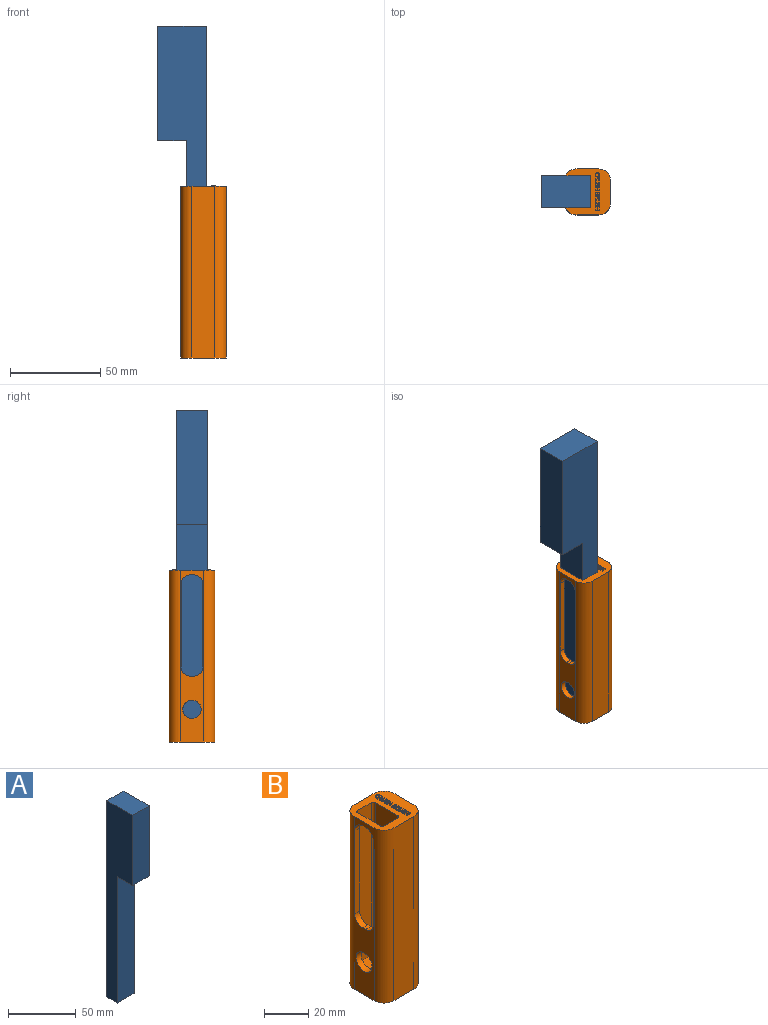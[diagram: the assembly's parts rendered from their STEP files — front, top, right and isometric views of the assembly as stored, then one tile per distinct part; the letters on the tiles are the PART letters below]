
ASSEMBLY  parts=2 mates=1
PART A: 8 faces, bbox 17.5x27x177.8 mm
  f0: plane 114.3x17.46mm, normal (0,-1,0), area 1996mm2, adj f1,f3,f5,f6
  f1: plane 177.8x26.99mm, normal (1,0,0), area 2983.9mm2, adj f0,f2,f4,f5,f6,f7
  f2: plane 177.8x17.46mm, normal (0,1,0), area 3104.8mm2, adj f1,f3,f4,f5
  f3: plane 177.8x26.99mm, normal (-1,0,0), area 2983.9mm2, adj f0,f2,f4,f5,f6,f7
  f4: plane 26.99x17.46mm, normal (0,0,1), area 471.3mm2, adj f1,f2,f3,f7
  f5: plane 17.46x11.11mm, normal (0,0,-1), area 194.1mm2, adj f0,f1,f2,f3
  f6: plane 17.46x15.88mm, normal (0,0,-1), area 277.2mm2, adj f0,f1,f3,f7
  f7: plane 63.5x17.46mm, normal (0,-1,0), area 1108.9mm2, adj f1,f3,f4,f6
PART B: 235 faces, bbox 25.4x25.4x95.8 mm
  f0: plane 95.25x12.7mm, normal (0,1,0), area 1137.1mm2, adj f1,f7,f33,f34,f228,f229,f230,f231
  f1: plane 25.4x25.4mm, normal (0,0,1), area 406.4mm2, adj f0,f3,f4,f5,f6,f8,f9,f10
  f2: cylinder r=1.91mm len=4.75mm, axis (1,0,0), area 56.9mm2, adj f6,f16
  f3: plane 95.25x12.7mm, normal (-1,0,0), area 479.9mm2, adj f1,f7,f12,f13,f14,f15,f27,f28
  f4: plane 84.14x14.48mm, normal (1,0,0), area 488.3mm2, adj f1,f11,f12,f13,f14,f15,f24,f25
  f5: plane 95.25x12.7mm, normal (0,-1,0), area 1209.7mm2, adj f1,f7,f31,f32
  f6: plane 95.25x12.7mm, normal (1,0,0), area 1198.3mm2, adj f1,f2,f7,f32,f33
  f7: plane 25.4x25.4mm, normal (0,0,-1), area 573.6mm2, adj f0,f3,f5,f6,f31,f32,f33,f34
  f8: plane 84.14x14.48mm, normal (-1,0,0), area 1157.3mm2, adj f1,f11,f17,f18,f19,f20,f21,f22
  f9: plane 84.14x8.59mm, normal (0,-1,0), area 722.3mm2, adj f1,f11,f23,f24
  f10: plane 84.14x8.59mm, normal (0,1,0), area 722.3mm2, adj f1,f11,f25,f26
  f11: plane 17.02x11.13mm, normal (0,0,1), area 187.9mm2, adj f4,f8,f9,f10,f23,f24,f25,f26
  f12: plane 3.18x1.78mm, normal (0,0,1), area 5.6mm2, adj f3,f4,f27,f28
  f13: plane 46.04x3.18mm, normal (0,-1,0), area 146.2mm2, adj f3,f4,f27,f29
  f14: plane 46.04x3.18mm, normal (0,1,0), area 146.2mm2, adj f3,f4,f28,f30
  f15: plane 3.18x1.78mm, normal (0,0,-1), area 5.6mm2, adj f3,f4,f29,f30
  f16: plane 9.68x8.38mm, normal (-1,0,0), area 49.4mm2, adj f2,f17,f18,f19,f20,f21,f22
  f17: plane 6.35x4.84mm, normal (0,1,0), area 30.7mm2, adj f8,f16,f18,f22
  f18: plane 6.35x4.19mm, normal (0,0.5,-0.87), area 30.7mm2, adj f8,f16,f17,f19
  f19: plane 6.35x4.19mm, normal (0,-0.5,-0.87), area 30.7mm2, adj f8,f16,f18,f20
  f20: plane 6.35x4.84mm, normal (0,-1,0), area 30.7mm2, adj f8,f16,f19,f21
  f21: plane 6.35x4.19mm, normal (0,-0.5,0.87), area 30.7mm2, adj f8,f16,f20,f22
  f22: plane 6.35x4.19mm, normal (0,0.5,0.87), area 30.7mm2, adj f8,f16,f17,f21
  f23: cylinder r=1.27mm len=84.14mm, axis (0,0,-1), area 167.8mm2, adj f1,f8,f9,f11
  f24: cylinder r=1.27mm len=84.14mm, axis (0,0,1), area 167.8mm2, adj f1,f4,f9,f11
  f25: cylinder r=1.27mm len=84.14mm, axis (0,0,-1), area 167.8mm2, adj f1,f4,f10,f11
  f26: cylinder r=1.27mm len=84.14mm, axis (0,0,1), area 167.8mm2, adj f1,f8,f10,f11
  f27: cylinder r=5.08mm len=5.08mm, axis (1,0,0), area 25.3mm2, adj f3,f4,f12,f13
  f28: cylinder r=5.08mm len=5.08mm, axis (-1,0,0), area 25.3mm2, adj f3,f4,f12,f14
  f29: cylinder r=5.08mm len=5.08mm, axis (-1,0,0), area 25.3mm2, adj f3,f4,f13,f15
  f30: cylinder r=5.08mm len=5.08mm, axis (1,0,0), area 25.3mm2, adj f3,f4,f14,f15
  f31: cylinder r=6.35mm len=95.25mm, axis (0,0,1), area 950.1mm2, adj f1,f3,f5,f7
  f32: cylinder r=6.35mm len=95.25mm, axis (0,0,-1), area 950.1mm2, adj f1,f5,f6,f7
  f33: cylinder r=6.35mm len=95.25mm, axis (0,0,1), area 950.1mm2, adj f0,f1,f6,f7
  f34: cylinder r=6.35mm len=95.25mm, axis (0,0,-1), area 950.1mm2, adj f0,f1,f3,f7
  f35: extruded ~0.58x0.51mm, area 0.3mm2, adj f1,f36,f49,f50
  f36: extruded ~0.51x0.51mm, area 0.3mm2, adj f1,f35,f37,f50
  f37: plane 0.51x0.22mm, normal (-0.44,-0.9,0), area 0.1mm2, adj f1,f36,f38,f50
  f38: extruded ~0.61x0.51mm, area 0.3mm2, adj f1,f37,f39,f50
  f39: extruded ~0.57x0.51mm, area 0.3mm2, adj f1,f38,f40,f50
  f40: extruded ~0.51x0.4mm, area 0.3mm2, adj f1,f39,f41,f50
  f41: extruded ~0.6x0.51mm, area 0.3mm2, adj f1,f40,f42,f50
  f42: extruded ~0.85x0.51mm, area 0.5mm2, adj f1,f41,f43,f50
  f43: extruded ~0.76x0.51mm, area 0.4mm2, adj f1,f42,f44,f50
  f44: extruded ~0.57x0.51mm, area 0.3mm2, adj f1,f43,f45,f50
  f45: plane 0.51x0.23mm, normal (0,-1,0), area 0.1mm2, adj f1,f44,f46,f50
  f46: extruded ~0.53x0.51mm, area 0.3mm2, adj f1,f45,f47,f50
  f47: extruded ~0.58x0.51mm, area 0.3mm2, adj f1,f46,f48,f50
  f48: extruded ~0.67x0.51mm, area 0.4mm2, adj f1,f47,f49,f50
  f49: extruded ~0.67x0.51mm, area 0.4mm2, adj f1,f35,f48,f50
  f50: plane 2.29x1.68mm, normal (0,0,1), area 1.1mm2, adj f35,f36,f37,f38,f39,f40,f41,f42
  f51: plane 0.51x0.35mm, normal (1,0,0), area 0.2mm2, adj f52,f68,f69,f70
  f52: plane 0.85x0.51mm, normal (0,-1,0), area 0.4mm2, adj f51,f53,f69,f70
  f53: plane 0.51x0.34mm, normal (-1,0,0), area 0.2mm2, adj f52,f54,f69,f70
  f54: extruded ~0.51x0.42mm, area 0.2mm2, adj f53,f55,f69,f70
  f55: extruded ~0.51x0.32mm, area 0.2mm2, adj f54,f56,f69,f70
  f56: extruded ~0.51x0.33mm, area 0.2mm2, adj f55,f68,f69,f70
  f57: plane 0.92x0.51mm, normal (0,-1,0), area 0.5mm2, adj f1,f58,f67,f69
  f58: plane 0.51x0.46mm, normal (-1,0,0), area 0.2mm2, adj f1,f57,f59,f69
  f59: plane 0.92x0.54mm, normal (-0.5,0.86,0), area 0.5mm2, adj f1,f58,f60,f69
  f60: plane 0.51x0.31mm, normal (-1,0,0), area 0.2mm2, adj f1,f59,f61,f69
  f61: plane 1x0.6mm, normal (0.52,-0.86,0), area 0.6mm2, adj f1,f60,f62,f69
  f62: extruded ~0.6x0.51mm, area 0.4mm2, adj f1,f61,f63,f69
  f63: extruded ~0.51x0.47mm, area 0.3mm2, adj f1,f62,f64,f69
  f64: extruded ~0.6x0.51mm, area 0.3mm2, adj f1,f63,f65,f69
  f65: plane 0.61x0.51mm, normal (1,0,0), area 0.3mm2, adj f1,f64,f66,f69
  f66: plane 2.22x0.51mm, normal (0,1,0), area 1.1mm2, adj f1,f65,f67,f69
  f67: plane 0.51x0.26mm, normal (-1,0,0), area 0.1mm2, adj f1,f57,f66,f69
  f68: extruded ~0.51x0.4mm, area 0.2mm2, adj f51,f56,f69,f70
  f69: plane 2.22x1.57mm, normal (0,0,1), area 1.5mm2, adj f51,f52,f53,f54,f55,f56,f57,f58
  f70: plane 0.88x0.85mm, normal (0,0,1), area 0.7mm2, adj f51,f52,f53,f54,f55,f56,f68
  f71: plane 1.44x0.51mm, normal (0,-1,0), area 0.7mm2, adj f1,f72,f84,f85
  f72: plane 0.51x0.26mm, normal (1,0,0), area 0.1mm2, adj f1,f71,f73,f85
  f73: plane 1.45x0.51mm, normal (0,1,0), area 0.7mm2, adj f1,f72,f74,f85
  f74: extruded ~0.51x0.43mm, area 0.2mm2, adj f1,f73,f75,f85
  f75: extruded ~0.51x0.43mm, area 0.2mm2, adj f1,f74,f76,f85
  f76: extruded ~0.51x0.45mm, area 0.2mm2, adj f1,f75,f77,f85
  f77: extruded ~0.51x0.43mm, area 0.2mm2, adj f1,f76,f78,f85
  f78: plane 1.45x0.51mm, normal (0,-1,0), area 0.7mm2, adj f1,f77,f79,f85
  f79: plane 0.51x0.26mm, normal (1,0,0), area 0.1mm2, adj f1,f78,f80,f85
  f80: plane 1.43x0.51mm, normal (0,1,0), area 0.7mm2, adj f1,f79,f81,f85
  f81: extruded ~0.6x0.51mm, area 0.3mm2, adj f1,f80,f82,f85
  f82: extruded ~0.62x0.51mm, area 0.3mm2, adj f1,f81,f83,f85
  f83: extruded ~0.63x0.51mm, area 0.3mm2, adj f1,f82,f84,f85
  f84: extruded ~0.6x0.51mm, area 0.3mm2, adj f1,f71,f83,f85
  f85: plane 2.25x1.7mm, normal (0,0,1), area 1.3mm2, adj f71,f72,f73,f74,f75,f76,f77,f78
  f86: extruded ~0.51x0.46mm, area 0.3mm2, adj f1,f87,f110,f111
  f87: extruded ~0.51x0.37mm, area 0.2mm2, adj f1,f86,f88,f111
  f88: extruded ~0.51x0.48mm, area 0.3mm2, adj f1,f87,f89,f111
  f89: extruded ~0.51x0.31mm, area 0.2mm2, adj f1,f88,f90,f111
  f90: extruded ~0.51x0.14mm, area 0.1mm2, adj f1,f89,f91,f111
  f91: extruded ~0.51x0.19mm, area 0.1mm2, adj f1,f90,f92,f111
  f92: extruded ~0.51x0.24mm, area 0.1mm2, adj f1,f91,f93,f111
  f93: extruded ~0.51x0.32mm, area 0.2mm2, adj f1,f92,f94,f111
  f94: extruded ~0.54x0.51mm, area 0.3mm2, adj f1,f93,f95,f111
  f95: plane 0.51x0.23mm, normal (-0.34,-0.94,0), area 0.1mm2, adj f1,f94,f96,f111
  f96: extruded ~0.61x0.51mm, area 0.3mm2, adj f1,f95,f97,f111
  f97: extruded ~0.51x0.51mm, area 0.3mm2, adj f1,f96,f98,f111
  f98: extruded ~0.51x0.41mm, area 0.2mm2, adj f1,f97,f99,f111
  f99: extruded ~0.51x0.4mm, area 0.2mm2, adj f1,f98,f100,f111
  f100: extruded ~0.51x0.44mm, area 0.3mm2, adj f1,f99,f101,f111
  f101: extruded ~0.51x0.33mm, area 0.2mm2, adj f1,f100,f102,f111
  f102: extruded ~0.51x0.16mm, area 0.1mm2, adj f1,f101,f103,f111
  f103: extruded ~0.51x0.19mm, area 0.1mm2, adj f1,f102,f104,f111
  f104: extruded ~0.51x0.27mm, area 0.2mm2, adj f1,f103,f105,f111
  f105: extruded ~0.51x0.39mm, area 0.2mm2, adj f1,f104,f106,f111
  f106: extruded ~0.51x0.32mm, area 0.2mm2, adj f1,f105,f107,f111
  f107: extruded ~0.51x0.3mm, area 0.2mm2, adj f1,f106,f108,f111
  f108: plane 0.51x0.25mm, normal (0,1,0), area 0.1mm2, adj f1,f107,f109,f111
  f109: extruded ~0.61x0.51mm, area 0.3mm2, adj f1,f108,f110,f111
  f110: extruded ~0.58x0.51mm, area 0.3mm2, adj f1,f86,f109,f111
  f111: plane 2.29x1.4mm, normal (0,0,1), area 1.1mm2, adj f86,f87,f88,f89,f90,f91,f92,f93
  f112: plane 0.51x0.26mm, normal (-1,0,0), area 0.1mm2, adj f1,f113,f123,f124
  f113: plane 2.22x0.51mm, normal (0,-1,0), area 1.1mm2, adj f1,f112,f114,f124
  f114: plane 0.51x0.26mm, normal (1,0,0), area 0.1mm2, adj f1,f113,f115,f124
  f115: plane 0.95x0.51mm, normal (0,1,0), area 0.5mm2, adj f1,f114,f116,f124
  f116: plane 1.17x0.51mm, normal (1,0,0), area 0.6mm2, adj f1,f115,f117,f124
  f117: plane 0.95x0.51mm, normal (0,-1,0), area 0.5mm2, adj f1,f116,f118,f124
  f118: plane 0.51x0.26mm, normal (1,0,0), area 0.1mm2, adj f1,f117,f119,f124
  f119: plane 2.22x0.51mm, normal (0,1,0), area 1.1mm2, adj f1,f118,f120,f124
  f120: plane 0.51x0.26mm, normal (-1,0,0), area 0.1mm2, adj f1,f119,f121,f124
  f121: plane 1.05x0.51mm, normal (0,-1,0), area 0.5mm2, adj f1,f120,f122,f124
  f122: plane 1.17x0.51mm, normal (-1,0,0), area 0.6mm2, adj f1,f121,f123,f124
  f123: plane 1.05x0.51mm, normal (0,1,0), area 0.5mm2, adj f1,f112,f122,f124
  f124: plane 2.22x1.69mm, normal (0,0,1), area 1.4mm2, adj f112,f113,f114,f115,f116,f117,f118,f119
  f125: plane 0.83x0.51mm, normal (0,-1,0), area 0.4mm2, adj f126,f149,f150,f151
  f126: plane 0.51x0.44mm, normal (-1,0,0), area 0.2mm2, adj f125,f127,f150,f151
  f127: extruded ~0.51x0.42mm, area 0.2mm2, adj f126,f128,f150,f151
  f128: extruded ~0.51x0.3mm, area 0.2mm2, adj f127,f129,f150,f151
  f129: extruded ~0.51x0.33mm, area 0.2mm2, adj f128,f130,f150,f151
  f130: extruded ~0.51x0.41mm, area 0.2mm2, adj f129,f149,f150,f151
  f131: plane 0.51x0.43mm, normal (1,0,0), area 0.2mm2, adj f132,f147,f150,f152
  f132: plane 0.73x0.51mm, normal (0,-1,0), area 0.4mm2, adj f131,f133,f150,f152
  f133: plane 0.51x0.38mm, normal (-1,0,0), area 0.2mm2, adj f132,f134,f150,f152
  f134: extruded ~0.51x0.43mm, area 0.2mm2, adj f133,f135,f150,f152
  f135: extruded ~0.51x0.27mm, area 0.2mm2, adj f134,f136,f150,f152
  f136: extruded ~0.51x0.29mm, area 0.2mm2, adj f135,f147,f150,f152
  f137: plane 0.63x0.51mm, normal (1,0,0), area 0.3mm2, adj f1,f138,f148,f150
  f138: plane 2.22x0.51mm, normal (0,1,0), area 1.1mm2, adj f1,f137,f139,f150
  f139: plane 0.78x0.51mm, normal (-1,0,0), area 0.4mm2, adj f1,f138,f140,f150
  f140: extruded ~0.56x0.51mm, area 0.3mm2, adj f1,f139,f141,f150
  f141: extruded ~0.51x0.47mm, area 0.3mm2, adj f1,f140,f142,f150
  f142: extruded ~0.53x0.51mm, area 0.4mm2, adj f1,f141,f143,f150
  f143: plane 0.51x0.02mm, normal (0,-1,0), area 0mm2, adj f1,f142,f144,f150
  f144: extruded ~0.51x0.32mm, area 0.2mm2, adj f1,f143,f145,f150
  f145: extruded ~0.51x0.33mm, area 0.2mm2, adj f1,f144,f146,f150
  f146: extruded ~0.51x0.42mm, area 0.2mm2, adj f1,f145,f148,f150
  f147: extruded ~0.51x0.39mm, area 0.2mm2, adj f131,f136,f150,f152
  f148: extruded ~0.64x0.51mm, area 0.3mm2, adj f1,f137,f146,f150
  f149: plane 0.51x0.46mm, normal (1,0,0), area 0.2mm2, adj f125,f130,f150,f151
  f150: plane 2.22x1.54mm, normal (0,0,1), area 1.7mm2, adj f125,f126,f127,f128,f129,f130,f131,f132
  f151: plane 1.01x0.83mm, normal (0,0,1), area 0.8mm2, adj f125,f126,f127,f128,f129,f130,f149
  f152: plane 0.94x0.73mm, normal (0,0,1), area 0.6mm2, adj f131,f132,f133,f134,f135,f136,f147
  f153: plane 0.51x0.35mm, normal (1,0,0), area 0.2mm2, adj f154,f170,f171,f172
  f154: plane 0.85x0.51mm, normal (0,-1,0), area 0.4mm2, adj f153,f155,f171,f172
  f155: plane 0.51x0.34mm, normal (-1,0,0), area 0.2mm2, adj f154,f156,f171,f172
  f156: extruded ~0.51x0.42mm, area 0.2mm2, adj f155,f157,f171,f172
  f157: extruded ~0.51x0.32mm, area 0.2mm2, adj f156,f158,f171,f172
  f158: extruded ~0.51x0.33mm, area 0.2mm2, adj f157,f170,f171,f172
  f159: plane 0.92x0.51mm, normal (0,-1,0), area 0.5mm2, adj f1,f160,f169,f171
  f160: plane 0.51x0.46mm, normal (-1,0,0), area 0.2mm2, adj f1,f159,f161,f171
  f161: plane 0.92x0.54mm, normal (-0.5,0.86,0), area 0.5mm2, adj f1,f160,f162,f171
  f162: plane 0.51x0.31mm, normal (-1,0,0), area 0.2mm2, adj f1,f161,f163,f171
  f163: plane 1x0.6mm, normal (0.52,-0.86,0), area 0.6mm2, adj f1,f162,f164,f171
  f164: extruded ~0.6x0.51mm, area 0.4mm2, adj f1,f163,f165,f171
  f165: extruded ~0.51x0.47mm, area 0.3mm2, adj f1,f164,f166,f171
  f166: extruded ~0.6x0.51mm, area 0.3mm2, adj f1,f165,f167,f171
  f167: plane 0.61x0.51mm, normal (1,0,0), area 0.3mm2, adj f1,f166,f168,f171
  f168: plane 2.22x0.51mm, normal (0,1,0), area 1.1mm2, adj f1,f167,f169,f171
  f169: plane 0.51x0.26mm, normal (-1,0,0), area 0.1mm2, adj f1,f159,f168,f171
  f170: extruded ~0.51x0.4mm, area 0.2mm2, adj f153,f158,f171,f172
  f171: plane 2.22x1.57mm, normal (0,0,1), area 1.5mm2, adj f153,f154,f155,f156,f157,f158,f159,f160
  f172: plane 0.88x0.85mm, normal (0,0,1), area 0.7mm2, adj f153,f154,f155,f156,f157,f158,f170
  f173: plane 1.44x0.51mm, normal (0,-1,0), area 0.7mm2, adj f1,f174,f186,f187
  f174: plane 0.51x0.26mm, normal (1,0,0), area 0.1mm2, adj f1,f173,f175,f187
  f175: plane 1.45x0.51mm, normal (0,1,0), area 0.7mm2, adj f1,f174,f176,f187
  f176: extruded ~0.51x0.43mm, area 0.2mm2, adj f1,f175,f177,f187
  f177: extruded ~0.51x0.43mm, area 0.2mm2, adj f1,f176,f178,f187
  f178: extruded ~0.51x0.45mm, area 0.2mm2, adj f1,f177,f179,f187
  f179: extruded ~0.51x0.43mm, area 0.2mm2, adj f1,f178,f180,f187
  f180: plane 1.45x0.51mm, normal (0,-1,0), area 0.7mm2, adj f1,f179,f181,f187
  f181: plane 0.51x0.26mm, normal (1,0,0), area 0.1mm2, adj f1,f180,f182,f187
  f182: plane 1.43x0.51mm, normal (0,1,0), area 0.7mm2, adj f1,f181,f183,f187
  f183: extruded ~0.6x0.51mm, area 0.3mm2, adj f1,f182,f184,f187
  f184: extruded ~0.62x0.51mm, area 0.3mm2, adj f1,f183,f185,f187
  f185: extruded ~0.63x0.51mm, area 0.3mm2, adj f1,f184,f186,f187
  f186: extruded ~0.6x0.51mm, area 0.3mm2, adj f1,f173,f185,f187
  f187: plane 2.25x1.7mm, normal (0,0,1), area 1.3mm2, adj f173,f174,f175,f176,f177,f178,f179,f180
  f188: extruded ~0.51x0.46mm, area 0.3mm2, adj f1,f189,f212,f213
  f189: extruded ~0.51x0.37mm, area 0.2mm2, adj f1,f188,f190,f213
  f190: extruded ~0.51x0.48mm, area 0.3mm2, adj f1,f189,f191,f213
  f191: extruded ~0.51x0.31mm, area 0.2mm2, adj f1,f190,f192,f213
  f192: extruded ~0.51x0.14mm, area 0.1mm2, adj f1,f191,f193,f213
  f193: extruded ~0.51x0.19mm, area 0.1mm2, adj f1,f192,f194,f213
  f194: extruded ~0.51x0.24mm, area 0.1mm2, adj f1,f193,f195,f213
  f195: extruded ~0.51x0.32mm, area 0.2mm2, adj f1,f194,f196,f213
  f196: extruded ~0.54x0.51mm, area 0.3mm2, adj f1,f195,f197,f213
  f197: plane 0.51x0.23mm, normal (-0.34,-0.94,0), area 0.1mm2, adj f1,f196,f198,f213
  f198: extruded ~0.61x0.51mm, area 0.3mm2, adj f1,f197,f199,f213
  f199: extruded ~0.51x0.51mm, area 0.3mm2, adj f1,f198,f200,f213
  f200: extruded ~0.51x0.41mm, area 0.2mm2, adj f1,f199,f201,f213
  f201: extruded ~0.51x0.4mm, area 0.2mm2, adj f1,f200,f202,f213
  f202: extruded ~0.51x0.44mm, area 0.3mm2, adj f1,f201,f203,f213
  f203: extruded ~0.51x0.33mm, area 0.2mm2, adj f1,f202,f204,f213
  f204: extruded ~0.51x0.16mm, area 0.1mm2, adj f1,f203,f205,f213
  f205: extruded ~0.51x0.19mm, area 0.1mm2, adj f1,f204,f206,f213
  f206: extruded ~0.51x0.27mm, area 0.2mm2, adj f1,f205,f207,f213
  f207: extruded ~0.51x0.39mm, area 0.2mm2, adj f1,f206,f208,f213
  f208: extruded ~0.51x0.32mm, area 0.2mm2, adj f1,f207,f209,f213
  f209: extruded ~0.51x0.3mm, area 0.2mm2, adj f1,f208,f210,f213
  f210: plane 0.51x0.25mm, normal (0,1,0), area 0.1mm2, adj f1,f209,f211,f213
  f211: extruded ~0.61x0.51mm, area 0.3mm2, adj f1,f210,f212,f213
  f212: extruded ~0.58x0.51mm, area 0.3mm2, adj f1,f188,f211,f213
  f213: plane 2.29x1.4mm, normal (0,0,1), area 1.1mm2, adj f188,f189,f190,f191,f192,f193,f194,f195
  f214: plane 0.51x0.26mm, normal (-1,0,0), area 0.1mm2, adj f1,f215,f225,f226
  f215: plane 2.22x0.51mm, normal (0,-1,0), area 1.1mm2, adj f1,f214,f216,f226
  f216: plane 0.51x0.26mm, normal (1,0,0), area 0.1mm2, adj f1,f215,f217,f226
  f217: plane 0.95x0.51mm, normal (0,1,0), area 0.5mm2, adj f1,f216,f218,f226
  f218: plane 1.17x0.51mm, normal (1,0,0), area 0.6mm2, adj f1,f217,f219,f226
  f219: plane 0.95x0.51mm, normal (0,-1,0), area 0.5mm2, adj f1,f218,f220,f226
  f220: plane 0.51x0.26mm, normal (1,0,0), area 0.1mm2, adj f1,f219,f221,f226
  f221: plane 2.22x0.51mm, normal (0,1,0), area 1.1mm2, adj f1,f220,f222,f226
  f222: plane 0.51x0.26mm, normal (-1,0,0), area 0.1mm2, adj f1,f221,f223,f226
  f223: plane 1.05x0.51mm, normal (0,-1,0), area 0.5mm2, adj f1,f222,f224,f226
  f224: plane 1.17x0.51mm, normal (-1,0,0), area 0.6mm2, adj f1,f223,f225,f226
  f225: plane 1.05x0.51mm, normal (0,1,0), area 0.5mm2, adj f1,f214,f224,f226
  f226: plane 2.22x1.69mm, normal (0,0,1), area 1.4mm2, adj f214,f215,f216,f217,f218,f219,f220,f221
  f227: cylinder r=5.08mm len=10.16mm, axis (-1,0,0), area 101.3mm2, adj f3,f4
  f228: plane 16.03x6.35mm, normal (-1,0,0), area 101.8mm2, adj f0,f229,f231,f233
  f229: plane 19.33x11.43mm, normal (0,0,1), area 165.2mm2, adj f0,f228,f230,f232,f233,f234
  f230: plane 16.03x6.35mm, normal (1,0,0), area 101.8mm2, adj f0,f229,f231,f234
  f231: plane 19.33x11.43mm, normal (0,0,-1), area 202.1mm2, adj f0,f228,f230,f233,f234
  f232: cylinder r=3.43mm len=6.86mm, axis (0,0,1), area 68.4mm2, adj f7,f229
  f233: plane 6.35x5.72mm, normal (-0.5,0.87,0), area 41.9mm2, adj f228,f229,f231,f234
  f234: plane 6.35x5.72mm, normal (0.5,0.87,0), area 41.9mm2, adj f229,f230,f231,f233
PLACE A rot(axis=(0,0,-1),90deg) t=(-3.96,0,6.24)mm
PLACE B at identity fixed
MATE slider B.f11 <-> A.f5  axis (0,0,1) through (-3.96,0,11.11)mm
